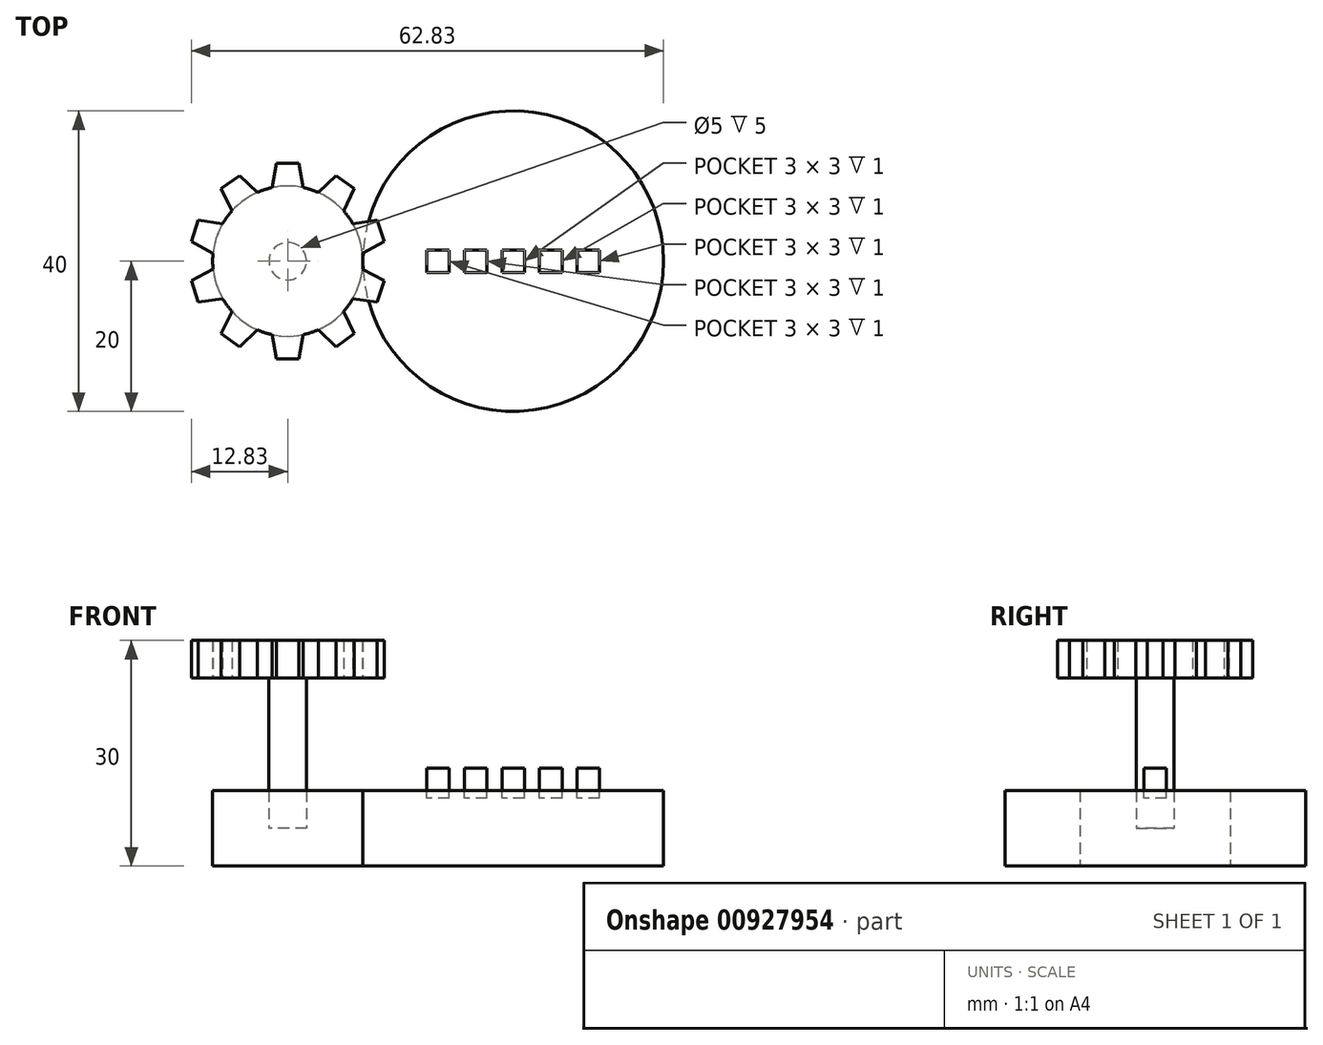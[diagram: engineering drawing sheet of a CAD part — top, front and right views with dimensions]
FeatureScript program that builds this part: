
annotation { "Feature Type Name" : "Feature", "Feature Type Description" : "" }
export const myFeature = defineFeature(function(context is Context, id is Id, definition is map)
    precondition{}
    {
        {
            var Q0;
            Q0=qCreatedBy(makeId("Top.planeOp"),FACE);
            var sketch = newSketch(context, id + "F0", { "sketchPlane" : qUnion([Q0])});
            skCircle(sketch, "E0", {"center": v(0, 0) * mm, "radius": 20 * mm});
            skCircle(sketch, "E1", {"center": v(-30, 0) * mm, "radius": 10 * mm});
            skSolve(sketch);
        }
        {
            var Q0;
            Q0 = qSketchRegion(id + "F0", true);
            extrude(context, id + "F1", {"entities" : qUnion([Q0]), "depth" : 10 * mm, "offsetDistance" : 25 * mm});
        }
        {
            var Q0;
            Q0=makeQuery(id+"F1.opExtrude","CAP_FACE",FACE,{"disambiguationData":[OSD([sQuery(id+"F0.wireOp",EDGE,"E1")])],"isStart":false});
            var sketch = newSketch(context, id + "F2", { "sketchPlane" : qUnion([Q0])});
            skCircle(sketch, "E2", {"center": v(-30, 0) * mm, "radius": 2.5 * mm});
            skSolve(sketch);
        }
        {
            var Q0;
            Q0 = qSketchRegion(id + "F2", true);
            extrude(context, id + "F3", {"entities" : qUnion([Q0]), "depth" : 15 * mm, "offsetDistance" : 25 * mm, "hasSecondDirection" : true, "secondDirectionOppositeDirection" : true, "secondDirectionDepth" : 5 * mm});
        }
        {
            var Q0;
            Q0=makeQuery(id+"F3.opExtrude","CAP_FACE",FACE,{"disambiguationData":[OSD([sQuery(id+"F2.wireOp",EDGE,"E2")])],"isStart":false});
            var sketch = newSketch(context, id + "F4", { "sketchPlane" : qUnion([Q0])});
            skCircle(sketch, "E3", {"center": v(-30, 0) * mm, "radius": 10 * mm});
            skLineSegment(sketch, "E4", {"start": v(-30, 13) * mm, "end": v(-28.5, 13) * mm});
            skLineSegment(sketch, "E5", {"start": v(-28.5, 13) * mm, "end": v(-27.93, 9.78) * mm});
            skLineSegment(sketch, "E6", {"start": v(-30, 0) * mm, "end": v(-30, 25) * mm, "construction": true});
            skLineSegment(sketch, "E7.MirrorCS", {"start": v(-31.5, 13) * mm, "end": v(-32.07, 9.78) * mm});
            skLineSegment(sketch, "E8.MirrorCS", {"start": v(-30, 13) * mm, "end": v(-31.5, 13) * mm});
            skLineSegment(sketch, "E9.1.0", {"start": v(-36.43, 11.4) * mm, "end": v(-34.08, 9.13) * mm});
            skLineSegment(sketch, "E9.1.1", {"start": v(-37.64, 10.52) * mm, "end": v(-36.43, 11.4) * mm});
            skLineSegment(sketch, "E9.1.2", {"start": v(-37.64, 10.52) * mm, "end": v(-38.85, 9.64) * mm});
            skLineSegment(sketch, "E9.1.3", {"start": v(-38.85, 9.64) * mm, "end": v(-37.42, 6.7) * mm});
            skLineSegment(sketch, "E9.2.0", {"start": v(-41.9, 5.44) * mm, "end": v(-38.67, 4.99) * mm});
            skLineSegment(sketch, "E9.2.1", {"start": v(-42.36, 4.02) * mm, "end": v(-41.9, 5.44) * mm});
            skLineSegment(sketch, "E9.2.2", {"start": v(-42.36, 4.02) * mm, "end": v(-42.83, 2.6) * mm});
            skLineSegment(sketch, "E9.2.3", {"start": v(-42.83, 2.6) * mm, "end": v(-39.94, 1.06) * mm});
            skLineSegment(sketch, "E10.2.3.0", {"start": v(-42.83, -2.6) * mm, "end": v(-39.94, -1.06) * mm});
            skLineSegment(sketch, "E10.3.3.0", {"start": v(-42.36, -4.02) * mm, "end": v(-42.83, -2.6) * mm});
            skLineSegment(sketch, "E10.6.3.0", {"start": v(-42.36, -4.02) * mm, "end": v(-41.9, -5.44) * mm});
            skLineSegment(sketch, "E10.9.3.0", {"start": v(-41.9, -5.44) * mm, "end": v(-38.67, -4.99) * mm});
            skLineSegment(sketch, "E10.2.4.0", {"start": v(-38.85, -9.64) * mm, "end": v(-37.42, -6.7) * mm});
            skLineSegment(sketch, "E10.3.4.0", {"start": v(-37.64, -10.52) * mm, "end": v(-38.85, -9.64) * mm});
            skLineSegment(sketch, "E10.6.4.0", {"start": v(-37.64, -10.52) * mm, "end": v(-36.43, -11.4) * mm});
            skLineSegment(sketch, "E10.9.4.0", {"start": v(-36.43, -11.4) * mm, "end": v(-34.08, -9.13) * mm});
            skLineSegment(sketch, "E10.2.5.0", {"start": v(-31.5, -13) * mm, "end": v(-32.07, -9.78) * mm});
            skLineSegment(sketch, "E10.3.5.0", {"start": v(-30, -13) * mm, "end": v(-31.5, -13) * mm});
            skLineSegment(sketch, "E10.6.5.0", {"start": v(-30, -13) * mm, "end": v(-28.5, -13) * mm});
            skLineSegment(sketch, "E10.9.5.0", {"start": v(-28.5, -13) * mm, "end": v(-27.93, -9.78) * mm});
            skLineSegment(sketch, "E10.2.6.0", {"start": v(-23.57, -11.4) * mm, "end": v(-25.92, -9.13) * mm});
            skLineSegment(sketch, "E10.3.6.0", {"start": v(-22.36, -10.52) * mm, "end": v(-23.57, -11.4) * mm});
            skLineSegment(sketch, "E10.6.6.0", {"start": v(-22.36, -10.52) * mm, "end": v(-21.15, -9.64) * mm});
            skLineSegment(sketch, "E10.9.6.0", {"start": v(-21.15, -9.64) * mm, "end": v(-22.58, -6.7) * mm});
            skLineSegment(sketch, "E10.2.7.0", {"start": v(-18.1, -5.44) * mm, "end": v(-21.33, -4.99) * mm});
            skLineSegment(sketch, "E10.3.7.0", {"start": v(-17.64, -4.02) * mm, "end": v(-18.1, -5.44) * mm});
            skLineSegment(sketch, "E10.6.7.0", {"start": v(-17.64, -4.02) * mm, "end": v(-17.17, -2.6) * mm});
            skLineSegment(sketch, "E10.9.7.0", {"start": v(-17.17, -2.6) * mm, "end": v(-20.06, -1.06) * mm});
            skLineSegment(sketch, "E10.2.8.0", {"start": v(-17.17, 2.6) * mm, "end": v(-20.06, 1.06) * mm});
            skLineSegment(sketch, "E10.3.8.0", {"start": v(-17.64, 4.02) * mm, "end": v(-17.17, 2.6) * mm});
            skLineSegment(sketch, "E10.6.8.0", {"start": v(-17.64, 4.02) * mm, "end": v(-18.1, 5.44) * mm});
            skLineSegment(sketch, "E10.9.8.0", {"start": v(-18.1, 5.44) * mm, "end": v(-21.33, 4.99) * mm});
            skLineSegment(sketch, "E10.2.9.0", {"start": v(-21.15, 9.64) * mm, "end": v(-22.58, 6.7) * mm});
            skLineSegment(sketch, "E10.3.9.0", {"start": v(-22.36, 10.52) * mm, "end": v(-21.15, 9.64) * mm});
            skLineSegment(sketch, "E10.6.9.0", {"start": v(-22.36, 10.52) * mm, "end": v(-23.57, 11.4) * mm});
            skLineSegment(sketch, "E10.9.9.0", {"start": v(-23.57, 11.4) * mm, "end": v(-25.92, 9.13) * mm});
            skSolve(sketch);
        }
        {
            var Q0;
            Q0 = qSketchRegion(id + "F4", true);
            extrude(context, id + "F5", {"entities" : qUnion([Q0]), "depth" : 5 * mm, "offsetDistance" : 25 * mm});
        }
        {
            var Q0;
            Q0=makeQuery(id+"F3.opExtrude","SWEPT_BODY",BODY,{"disambiguationData":[OSD([sQuery(id+"F2.wireOp",EDGE,"E2")])]});
            var Q1;
            Q1=makeQuery(id+"F1.opExtrude","SWEPT_BODY",BODY,{"disambiguationData":[OSD([sQuery(id+"F0.wireOp",EDGE,"E1")])]});
            booleanBodies(context, id + "F6", {"operationType" : BooleanOperationType.SUBTRACTION, "tools" : qUnion([Q0]), "targets" : qUnion([Q1]), "keepTools" : true});
        }
        {
            var Q0;
            Q0=makeQuery(id+"F1.opExtrude","CAP_FACE",FACE,{"disambiguationData":[OSD([sQuery(id+"F0.wireOp",EDGE,"E0")])],"isStart":false});
            var sketch = newSketch(context, id + "F7", { "sketchPlane" : qUnion([Q0])});
            skLineSegment(sketch, "E11.bottom", {"start": v(1.5, 1.5) * mm, "end": v(-1.5, 1.5) * mm});
            skLineSegment(sketch, "E11.top", {"start": v(1.5, -1.5) * mm, "end": v(-1.5, -1.5) * mm});
            skLineSegment(sketch, "E11.left", {"start": v(1.5, 1.5) * mm, "end": v(1.5, -1.5) * mm});
            skLineSegment(sketch, "E11.right", {"start": v(-1.5, 1.5) * mm, "end": v(-1.5, -1.5) * mm});
            skPoint(sketch, "E11.middle", {"position": v(0, 0) * mm});
            skLineSegment(sketch, "E12.1.0.0", {"start": v(6.5, 1.5) * mm, "end": v(6.5, -1.5) * mm});
            skLineSegment(sketch, "E12.1.0.1", {"start": v(6.5, 1.5) * mm, "end": v(3.5, 1.5) * mm});
            skLineSegment(sketch, "E12.1.0.2", {"start": v(3.5, 1.5) * mm, "end": v(3.5, -1.5) * mm});
            skLineSegment(sketch, "E12.1.0.3", {"start": v(6.5, -1.5) * mm, "end": v(3.5, -1.5) * mm});
            skLineSegment(sketch, "E12.2.0.0", {"start": v(11.5, 1.5) * mm, "end": v(11.5, -1.5) * mm});
            skLineSegment(sketch, "E12.2.0.1", {"start": v(11.5, 1.5) * mm, "end": v(8.5, 1.5) * mm});
            skLineSegment(sketch, "E12.2.0.2", {"start": v(8.5, 1.5) * mm, "end": v(8.5, -1.5) * mm});
            skLineSegment(sketch, "E12.2.0.3", {"start": v(11.5, -1.5) * mm, "end": v(8.5, -1.5) * mm});
            skLineSegment(sketch, "E12.direction1", {"start": v(1.5, -1.5) * mm, "end": v(6.5, -1.5) * mm, "construction": true});
            skLineSegment(sketch, "E13.1.0.0", {"start": v(-6.5, 1.5) * mm, "end": v(-6.5, -1.5) * mm});
            skLineSegment(sketch, "E13.1.0.1", {"start": v(-3.5, 1.5) * mm, "end": v(-6.5, 1.5) * mm});
            skLineSegment(sketch, "E13.1.0.2", {"start": v(-3.5, -1.5) * mm, "end": v(-6.5, -1.5) * mm});
            skLineSegment(sketch, "E13.1.0.3", {"start": v(-3.5, 1.5) * mm, "end": v(-3.5, -1.5) * mm});
            skLineSegment(sketch, "E13.2.0.0", {"start": v(-11.5, 1.5) * mm, "end": v(-11.5, -1.5) * mm});
            skLineSegment(sketch, "E13.2.0.1", {"start": v(-8.5, 1.5) * mm, "end": v(-11.5, 1.5) * mm});
            skLineSegment(sketch, "E13.2.0.2", {"start": v(-8.5, -1.5) * mm, "end": v(-11.5, -1.5) * mm});
            skLineSegment(sketch, "E13.2.0.3", {"start": v(-8.5, 1.5) * mm, "end": v(-8.5, -1.5) * mm});
            skLineSegment(sketch, "E13.direction1", {"start": v(-1.5, -1.5) * mm, "end": v(-6.5, -1.5) * mm, "construction": true});
            skSolve(sketch);
        }
        {
            var Q0;
            Q0 = qSketchRegion(id + "F7", true);
            extrude(context, id + "F8", {"entities" : qUnion([Q0]), "operationType" : NewBodyOperationType.REMOVE, "oppositeDirection" : true, "depth" : 1 * mm, "offsetDistance" : 25 * mm});
        }
        {
            var Q0;
            Q0 = qSketchRegion(id + "F7", true);
            extrude(context, id + "F9", {"entities" : qUnion([Q0]), "depth" : 3 * mm, "offsetDistance" : 25 * mm});
        }
    });
